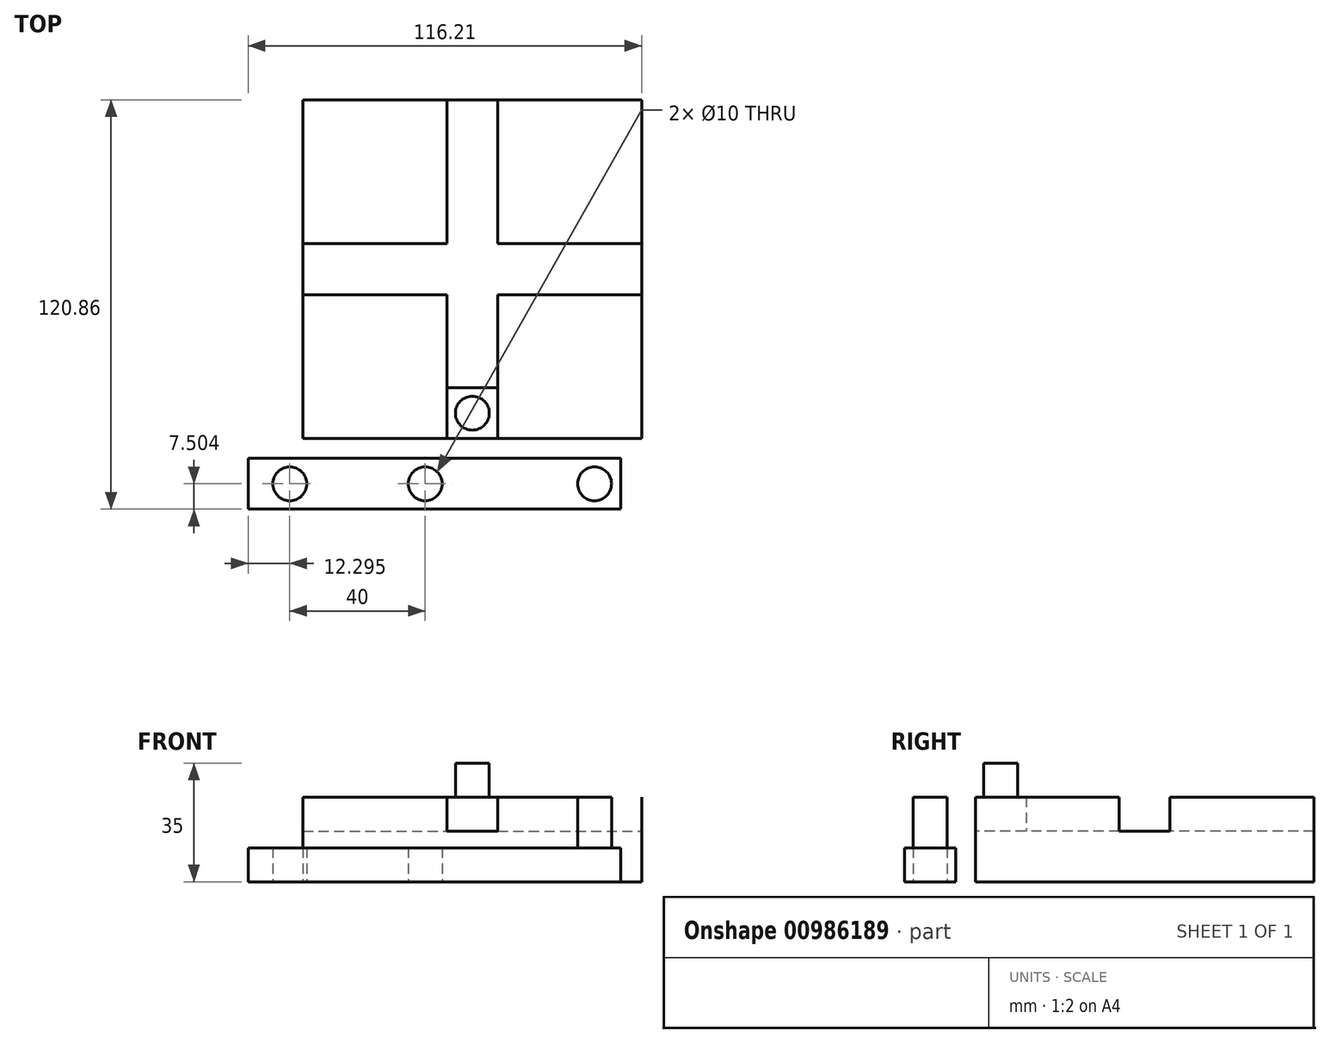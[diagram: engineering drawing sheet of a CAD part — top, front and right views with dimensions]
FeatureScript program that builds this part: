
annotation { "Feature Type Name" : "Feature", "Feature Type Description" : "" }
export const myFeature = defineFeature(function(context is Context, id is Id, definition is map)
    precondition{}
    {
        {
            var Q0;
            Q0=qCreatedBy(makeId("Top.planeOp"),FACE);
            var sketch = newSketch(context, id + "F0", { "sketchPlane" : qUnion([Q0])});
            skLineSegment(sketch, "E0.bottom", {"start": v(-50, 50) * mm, "end": v(50, 50) * mm});
            skLineSegment(sketch, "E0.top", {"start": v(-50, -50) * mm, "end": v(50, -50) * mm});
            skLineSegment(sketch, "E0.left", {"start": v(-50, 50) * mm, "end": v(-50, -50) * mm});
            skLineSegment(sketch, "E0.right", {"start": v(50, 50) * mm, "end": v(50, -50) * mm});
            skPoint(sketch, "E0.middle", {"position": v(0, 0) * mm});
            skSolve(sketch);
        }
        {
            var Q0;
            Q0 = qSketchRegion(id + "F0", true);
            extrude(context, id + "F1", {"entities" : qUnion([Q0]), "depth" : 25 * mm, "offsetDistance" : 25 * mm});
        }
        {
            var Q0;
            Q0=makeQuery(id+"F1.opExtrude","SWEPT_FACE",FACE,{"disambiguationData":[OSD([sQuery(id+"F0.wireOp",EDGE,"E0.top")])]});
            var sketch = newSketch(context, id + "F2", { "sketchPlane" : qUnion([Q0])});
            skLineSegment(sketch, "E1.bottom", {"start": v(7.5, 15) * mm, "end": v(-7.5, 15) * mm});
            skLineSegment(sketch, "E1.top", {"start": v(7.5, 35) * mm, "end": v(-7.5, 35) * mm});
            skLineSegment(sketch, "E1.left", {"start": v(7.5, 15) * mm, "end": v(7.5, 35) * mm});
            skLineSegment(sketch, "E1.right", {"start": v(-7.5, 15) * mm, "end": v(-7.5, 35) * mm});
            skPoint(sketch, "E1.middle", {"position": v(0, 25) * mm});
            skSolve(sketch);
        }
        {
            var Q0;
            Q0 = qSketchRegion(id + "F2", true);
            extrude(context, id + "F3", {"entities" : qUnion([Q0]), "operationType" : NewBodyOperationType.REMOVE, "oppositeDirection" : true, "depth" : 100 * mm, "offsetDistance" : 25 * mm});
        }
        {
            var Q0;
            Q0=makeQuery(id+"F1.opExtrude","SWEPT_FACE",FACE,{"disambiguationData":[OSD([sQuery(id+"F0.wireOp",EDGE,"E0.right")])]});
            var sketch = newSketch(context, id + "F4", { "sketchPlane" : qUnion([Q0])});
            skLineSegment(sketch, "E2.bottom", {"start": v(-7.5, 35) * mm, "end": v(7.5, 35) * mm});
            skLineSegment(sketch, "E2.top", {"start": v(-7.5, 15) * mm, "end": v(7.5, 15) * mm});
            skLineSegment(sketch, "E2.left", {"start": v(-7.5, 35) * mm, "end": v(-7.5, 15) * mm});
            skLineSegment(sketch, "E2.right", {"start": v(7.5, 35) * mm, "end": v(7.5, 15) * mm});
            skPoint(sketch, "E2.middle", {"position": v(0, 25) * mm});
            skSolve(sketch);
        }
        {
            var Q0;
            Q0 = qSketchRegion(id + "F4", true);
            extrude(context, id + "F5", {"entities" : qUnion([Q0]), "operationType" : NewBodyOperationType.REMOVE, "oppositeDirection" : true, "depth" : 100 * mm, "offsetDistance" : 25 * mm});
        }
        {
            var Q0;
            Q0=makeQuery(id+"F5.boolean.opBoolean","MERGE",FACE,{"derivedFrom":[makeQuery(id+"F3.boolean.opBoolean","COPY",FACE,{"derivedFrom":makeQuery(id+"F3.opExtrude","SWEPT_FACE",FACE,{"disambiguationData":[OSD([sQuery(id+"F2.wireOp",EDGE,"E1.bottom")])]})})],"fromTools":[makeQuery(id+"F5.opExtrude","SWEPT_FACE",FACE,{"disambiguationData":[OSD([sQuery(id+"F4.wireOp",EDGE,"E2.top")])]})]});
            var sketch = newSketch(context, id + "F6", { "sketchPlane" : qUnion([Q0])});
            skLineSegment(sketch, "E3.bottom", {"start": v(-7.5, -50) * mm, "end": v(7.5, -50) * mm});
            skLineSegment(sketch, "E3.top", {"start": v(-7.5, -35) * mm, "end": v(7.5, -35) * mm});
            skLineSegment(sketch, "E3.left", {"start": v(-7.5, -50) * mm, "end": v(-7.5, -35) * mm});
            skLineSegment(sketch, "E3.right", {"start": v(7.5, -50) * mm, "end": v(7.5, -35) * mm});
            skSolve(sketch);
        }
        {
            var Q0;
            Q0 = qSketchRegion(id + "F6", true);
            extrude(context, id + "F7", {"entities" : qUnion([Q0]), "depth" : 10 * mm, "offsetDistance" : 25 * mm});
        }
        {
            var Q0;
            Q0=makeQuery(id+"F7.opExtrude","CAP_FACE",FACE,{"disambiguationData":[OSD([sQuery(id+"F6.wireOp",EDGE,"E3.bottom"),sQuery(id+"F6.wireOp",EDGE,"E3.top"),sQuery(id+"F6.wireOp",EDGE,"E3.left"),sQuery(id+"F6.wireOp",EDGE,"E3.right")])],"isStart":false});
            var sketch = newSketch(context, id + "F8", { "sketchPlane" : qUnion([Q0])});
            skCircle(sketch, "E4", {"center": v(0, -42.5) * mm, "radius": 5 * mm});
            skPoint(sketch, "E4.centerSnap0", {"position": v(7.5, -42.5) * mm});
            skSolve(sketch);
        }
        {
            var Q0;
            Q0=makeQuery(id+"F8.imprint","IMPRINT",FACE,{"disambiguationData":[TD([[makeQuery(id+"F8.imprint","IMPRINT",EDGE,{"derivedFrom":sQuery(id+"F8.wireOp",EDGE,"E4")}),1.0]])]});
            extrude(context, id + "F9", {"entities" : qUnion([Q0]), "operationType" : NewBodyOperationType.ADD, "depth" : 10 * mm, "offsetDistance" : 25 * mm});
        }
        {
            var Q0;
            Q0=qCreatedBy(makeId("Top.planeOp"),FACE);
            var sketch = newSketch(context, id + "F10", { "sketchPlane" : qUnion([Q0])});
            skLineSegment(sketch, "E5.bottom", {"start": v(-66.21, -55.86) * mm, "end": v(43.79, -55.86) * mm});
            skLineSegment(sketch, "E5.top", {"start": v(-66.21, -70.86) * mm, "end": v(43.79, -70.86) * mm});
            skLineSegment(sketch, "E5.left", {"start": v(-66.21, -55.86) * mm, "end": v(-66.21, -70.86) * mm});
            skLineSegment(sketch, "E5.right", {"start": v(43.79, -55.86) * mm, "end": v(43.79, -70.86) * mm});
            skCircle(sketch, "E6", {"center": v(-53.91, -63.36) * mm, "radius": 5 * mm});
            skCircle(sketch, "E7", {"center": v(-13.91, -63.36) * mm, "radius": 5 * mm});
            skCircle(sketch, "E8", {"center": v(36.09, -63.36) * mm, "radius": 5 * mm});
            skSolve(sketch);
        }
        {
            var Q0;
            Q0=makeQuery(id+"F10.imprint","IMPRINT",FACE,{"disambiguationData":[TD([[makeQuery(id+"F10.imprint","IMPRINT",EDGE,{"derivedFrom":sQuery(id+"F10.wireOp",EDGE,"E5.bottom")}),-1.0]])]});
            var Q1;
            Q1=makeQuery(id+"F10.imprint","IMPRINT",FACE,{"disambiguationData":[TD([[makeQuery(id+"F10.imprint","IMPRINT",EDGE,{"derivedFrom":sQuery(id+"F10.wireOp",EDGE,"E8")}),1.0]])]});
            extrude(context, id + "F11", {"entities" : qUnion([Q0, Q1]), "depth" : 10 * mm, "offsetDistance" : 25 * mm});
        }
        {
            var Q0;
            Q0=makeQuery(id+"F10.imprint","IMPRINT",FACE,{"disambiguationData":[TD([[makeQuery(id+"F10.imprint","IMPRINT",EDGE,{"derivedFrom":sQuery(id+"F10.wireOp",EDGE,"E8")}),1.0]])]});
            extrude(context, id + "F12", {"entities" : qUnion([Q0]), "operationType" : NewBodyOperationType.ADD, "depth" : 25 * mm, "offsetDistance" : 25 * mm});
        }
    });
